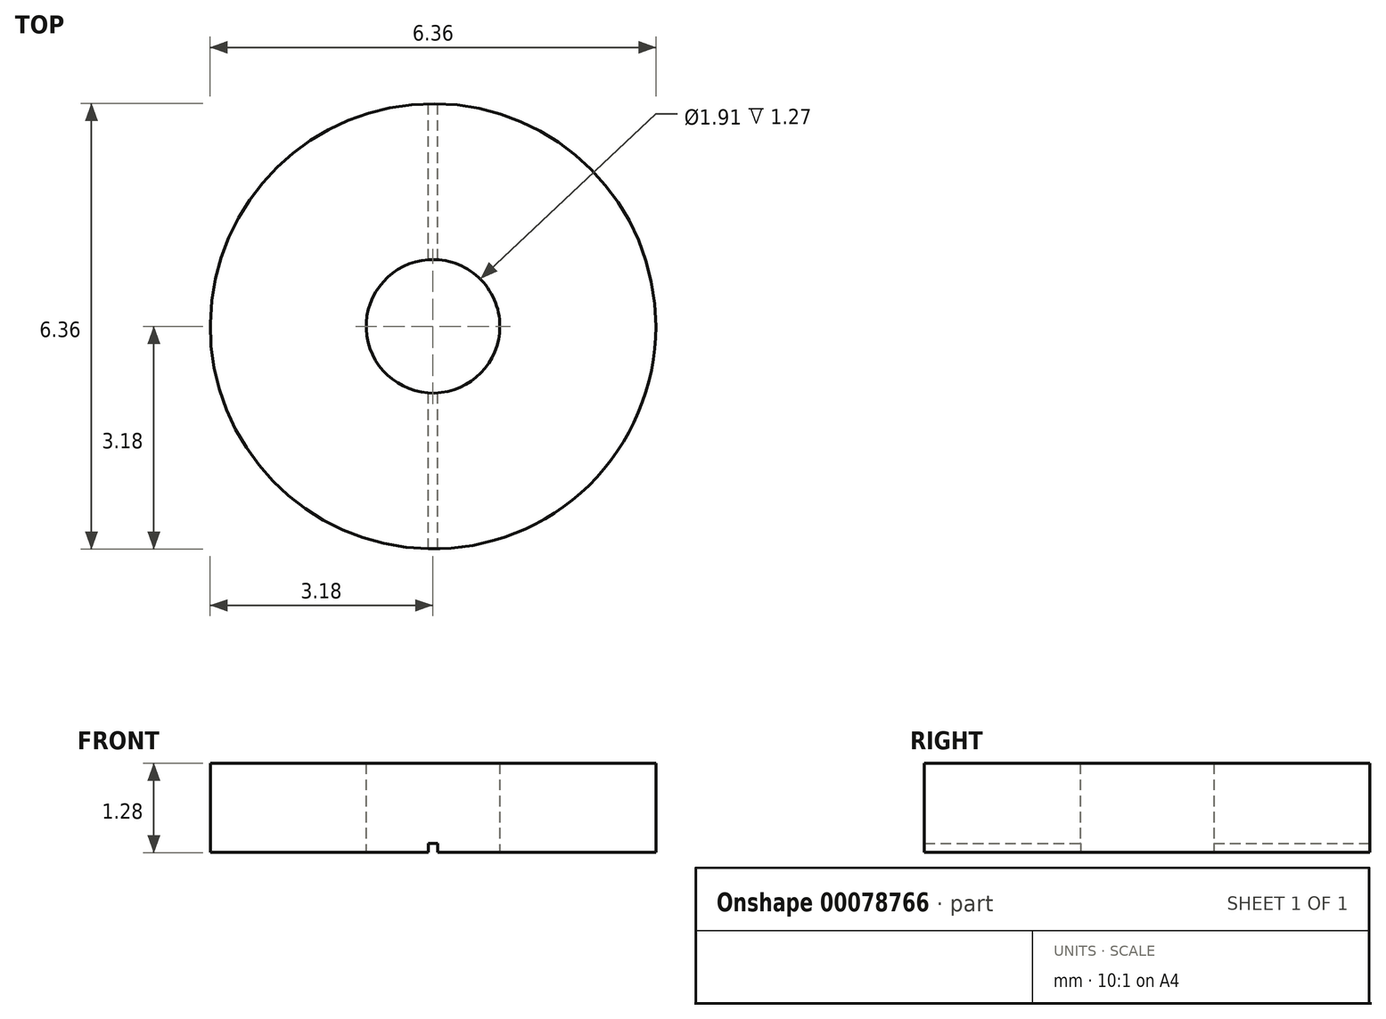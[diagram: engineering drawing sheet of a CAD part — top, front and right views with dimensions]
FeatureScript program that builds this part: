
annotation { "Feature Type Name" : "Feature", "Feature Type Description" : "" }
export const myFeature = defineFeature(function(context is Context, id is Id, definition is map)
    precondition{}
    {
        {
            var Q0;
            Q0=qCreatedBy(makeId("Top.planeOp"),FACE);
            var sketch = newSketch(context, id + "F0", { "sketchPlane" : qUnion([Q0])});
            skCircle(sketch, "E0", {"center": v(0, 0) * mm, "radius": 3.18 * mm});
            skCircle(sketch, "E1", {"center": v(0, 0) * mm, "radius": 0.95 * mm});
            skSolve(sketch);
        }
        {
            var Q0;
            Q0=makeQuery(id+"F0.imprint","IMPRINT",FACE,{"disambiguationData":[TD([[makeQuery(id+"F0.imprint","IMPRINT",EDGE,{"derivedFrom":sQuery(id+"F0.wireOp",EDGE,"E0")}),1.0]])]});
            extrude(context, id + "F1", {"entities" : qUnion([Q0]), "depth" : 1.27 * mm, "symmetric" : true});
        }
        {
            var Q0;
            Q0=makeQuery(id+"F1.opExtrude","CAP_FACE",FACE,{"disambiguationData":[OSD([sQuery(id+"F0.wireOp",EDGE,"E0"),sQuery(id+"F0.wireOp",EDGE,"E1")])],"isStart":true});
            var sketch = newSketch(context, id + "F2", { "sketchPlane" : qUnion([Q0])});
            skLineSegment(sketch, "E2.bottom", {"start": v(0.06, 3.81) * mm, "end": v(-0.06, 3.81) * mm});
            skLineSegment(sketch, "E2.top", {"start": v(0.06, -3.8) * mm, "end": v(-0.06, -3.8) * mm});
            skLineSegment(sketch, "E2.left", {"start": v(0.06, 3.81) * mm, "end": v(0.06, -3.8) * mm});
            skLineSegment(sketch, "E2.right", {"start": v(-0.06, 3.81) * mm, "end": v(-0.06, -3.8) * mm});
            skPoint(sketch, "E2.middle", {"position": v(0, 0) * mm});
            skSolve(sketch);
        }
        {
            var Q0;
            {var subQ0=sQuery(id+"F2.wireOp",EDGE,"E2.left");var subQ1=makeQuery(id+"F1.opExtrude","CAP_EDGE",EDGE,{"disambiguationData":[OSD([sQuery(id+"F0.wireOp",EDGE,"E0")])],"isStart":true});var subQ2=makeQuery(id+"F2.imprint","INTERSECT",VERTEX,{"disambiguationData":[OD(0.0)],"derivedFrom":[subQ1,subQ0]});Q0=makeQuery(id+"F2.imprint","IMPRINT",FACE,{"disambiguationData":[TD([[makeQuery(id+"F2.imprint","IMPRINT",EDGE,{"disambiguationData":[TD([[subQ2,-1.0]])],"derivedFrom":subQ0}),-1.0]])]});}
            var Q1;
            {var subQ0=sQuery(id+"F2.wireOp",EDGE,"E2.left");var subQ1=makeQuery(id+"F1.opExtrude","CAP_EDGE",EDGE,{"disambiguationData":[OSD([sQuery(id+"F0.wireOp",EDGE,"E0")])],"isStart":true});var subQ2=makeQuery(id+"F2.imprint","INTERSECT",VERTEX,{"disambiguationData":[OD(1.0)],"derivedFrom":[subQ1,subQ0]});Q1=makeQuery(id+"F2.imprint","IMPRINT",FACE,{"disambiguationData":[TD([[makeQuery(id+"F2.imprint","IMPRINT",EDGE,{"disambiguationData":[TD([[subQ2,1.0]])],"derivedFrom":subQ0}),-1.0]])]});}
            var Q2;
            {var subQ0=sQuery(id+"F2.wireOp",EDGE,"E2.top");Q2=makeQuery(id+"F2.imprint","IMPRINT",FACE,{"disambiguationData":[TD([[makeQuery(id+"F2.imprint","IMPRINT",EDGE,{"derivedFrom":subQ0}),-1.0]])]});}
            var Q3;
            {var subQ0=sQuery(id+"F2.wireOp",EDGE,"E2.left");var subQ1=makeQuery(id+"F1.opExtrude","CAP_EDGE",EDGE,{"disambiguationData":[OSD([sQuery(id+"F0.wireOp",EDGE,"E1")])],"isStart":true});var subQ2=makeQuery(id+"F2.imprint","INTERSECT",VERTEX,{"disambiguationData":[OD(0.0)],"derivedFrom":[subQ1,subQ0]});Q3=makeQuery(id+"F2.imprint","IMPRINT",FACE,{"disambiguationData":[TD([[makeQuery(id+"F2.imprint","IMPRINT",EDGE,{"disambiguationData":[TD([[subQ2,-1.0]])],"derivedFrom":subQ0}),-1.0]])]});}
            var Q4;
            {var subQ0=sQuery(id+"F2.wireOp",EDGE,"E2.bottom");Q4=makeQuery(id+"F2.imprint","IMPRINT",FACE,{"disambiguationData":[TD([[makeQuery(id+"F2.imprint","IMPRINT",EDGE,{"derivedFrom":subQ0}),1.0]])]});}
            extrude(context, id + "F3", {"entities" : qUnion([Q0, Q1, Q2, Q3, Q4]), "operationType" : NewBodyOperationType.REMOVE, "oppositeDirection" : true, "depth" : 0.13 * mm});
        }
    });
